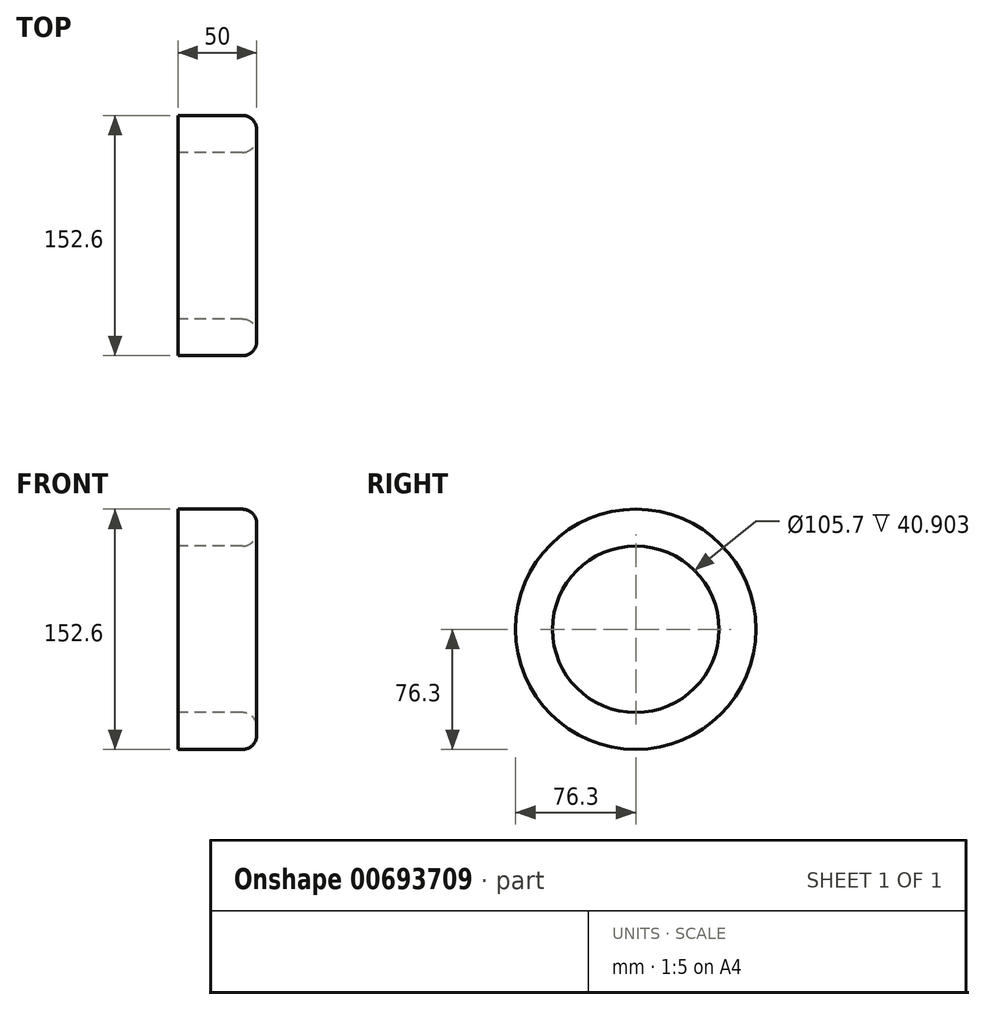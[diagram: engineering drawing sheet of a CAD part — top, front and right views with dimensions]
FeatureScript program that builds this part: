
annotation { "Feature Type Name" : "Feature", "Feature Type Description" : "" }
export const myFeature = defineFeature(function(context is Context, id is Id, definition is map)
    precondition{}
    {
        {
            var Q0;
            Q0=qCreatedBy(makeId("Right.planeOp"),FACE);
            var sketch = newSketch(context, id + "F0", { "sketchPlane" : qUnion([Q0])});
            skCircle(sketch, "E0", {"center": v(0, 0) * mm, "radius": 52.85 * mm});
            skCircle(sketch, "E1", {"center": v(114.27, -38.75) * mm, "radius": 115.84 * mm});
            skCircle(sketch, "E2", {"center": v(0, 0) * mm, "radius": 76.3 * mm});
            skSolve(sketch);
        }
        {
            var Q0;
            {var subQ0=sQuery(id+"F0.wireOp",EDGE,"E1");var subQ1=sQuery(id+"F0.wireOp",EDGE,"E0");var subQ2=makeQuery(id+"F0.imprint","INTERSECT",VERTEX,{"disambiguationData":[OD(0.0)],"derivedFrom":[subQ1,subQ0]});Q0=makeQuery(id+"F0.imprint","IMPRINT",FACE,{"disambiguationData":[TD([[makeQuery(id+"F0.imprint","IMPRINT",EDGE,{"disambiguationData":[TD([[subQ2,-1.0]])],"derivedFrom":subQ1}),-1.0]])]});}
            var Q1;
            {var subQ0=sQuery(id+"F0.wireOp",EDGE,"E1");var subQ1=sQuery(id+"F0.wireOp",EDGE,"E0");var subQ2=makeQuery(id+"F0.imprint","INTERSECT",VERTEX,{"disambiguationData":[OD(0.0)],"derivedFrom":[subQ1,subQ0]});Q1=makeQuery(id+"F0.imprint","IMPRINT",FACE,{"disambiguationData":[TD([[makeQuery(id+"F0.imprint","IMPRINT",EDGE,{"disambiguationData":[TD([[subQ2,1.0]])],"derivedFrom":subQ1}),-1.0]])]});}
            extrude(context, id + "F1", {"entities" : qUnion([Q0, Q1]), "depth" : 50 * mm, "offsetDistance" : 25 * mm});
        }
        {
            var Q0;
            Q0=makeQuery(id+"F1.opExtrude","CAP_EDGE",EDGE,{"disambiguationData":[OSD([sQuery(id+"F0.wireOp",EDGE,"E2")])],"isStart":false});
            var Q1;
            Q1=makeQuery(id+"F1.opExtrude","CAP_EDGE",EDGE,{"disambiguationData":[OSD([sQuery(id+"F0.wireOp",EDGE,"E0")])],"isStart":false});
            fillet(context, id + "F2", {"entities" : qUnion([Q0, Q1]), "radius" : 9.1 * mm, "tangentPropagation" : true, "allowEdgeOverflow" : false});
        }
        {
            var Q0;
            Q0=qCreatedBy(makeId("Front.planeOp"),FACE);
            var sketch = newSketch(context, id + "F3", { "sketchPlane" : qUnion([Q0])});
            skCircle(sketch, "E3", {"center": v(54.81, 22.76) * mm, "radius": 49.36 * mm});
            skCircle(sketch, "E4", {"center": v(77.82, 0) * mm, "radius": 9.18 * mm});
            skCircle(sketch, "E5", {"center": v(15.46, -78.07) * mm, "radius": 4.1 * mm});
            skSolve(sketch);
        }
    });
